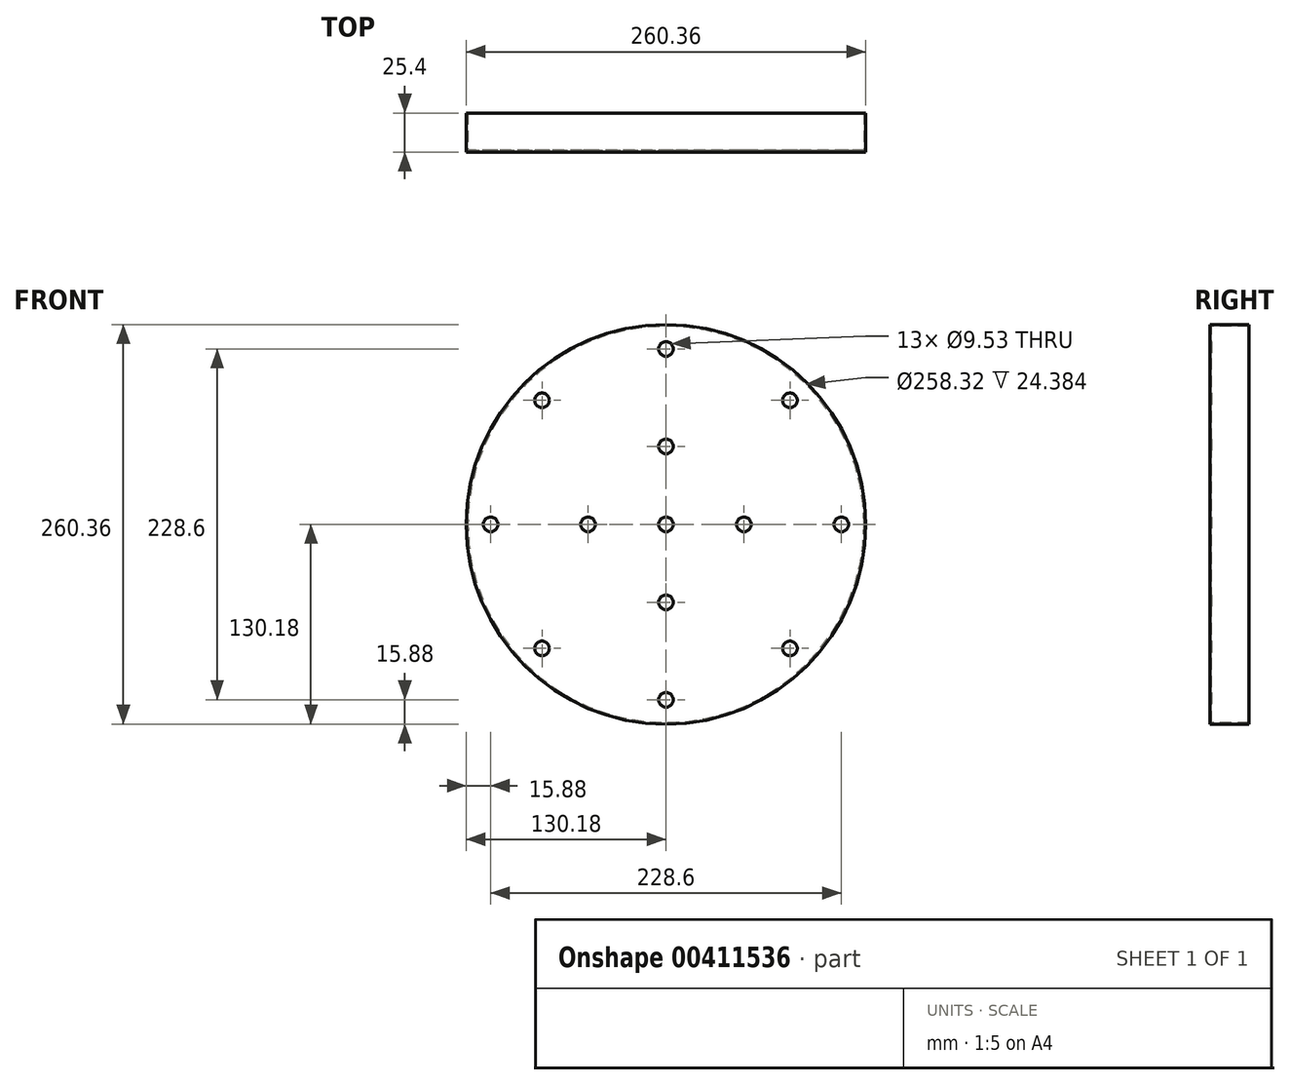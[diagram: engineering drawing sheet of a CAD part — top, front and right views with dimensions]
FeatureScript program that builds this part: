
annotation { "Feature Type Name" : "Feature", "Feature Type Description" : "" }
export const myFeature = defineFeature(function(context is Context, id is Id, definition is map)
    precondition{}
    {
        {
            var Q0;
            Q0=qCreatedBy(makeId("Top.planeOp"),FACE);
            var sketch = newSketch(context, id + "F0", { "sketchPlane" : qUnion([Q0])});
            skLineSegment(sketch, "E0.bottom", {"start": v(0, 0) * mm, "end": v(130.18, 0) * mm});
            skLineSegment(sketch, "E0.top", {"start": v(0, 1.02) * mm, "end": v(129.16, 1.02) * mm});
            skLineSegment(sketch, "E0.left", {"start": v(0, 0) * mm, "end": v(0, 1.02) * mm});
            skLineSegment(sketch, "E1.top", {"start": v(130.18, 25.4) * mm, "end": v(129.16, 25.4) * mm});
            skLineSegment(sketch, "E1.right", {"start": v(129.16, 1.02) * mm, "end": v(129.16, 25.4) * mm});
            skLineSegment(sketch, "E2", {"start": v(130.18, 25.4) * mm, "end": v(130.18, 0) * mm});
            skSolve(sketch);
        }
        {
            var Q0;
            Q0=makeQuery(id+"F0.imprint","IMPRINT",FACE,{"disambiguationData":[TD([[makeQuery(id+"F0.imprint","IMPRINT",EDGE,{"derivedFrom":sQuery(id+"F0.wireOp",EDGE,"E0.bottom")}),1.0]])]});
            var Q1;
            Q1=sQuery(id+"F0.wireOp",EDGE,"E0.left");
            revolve(context, id + "F1", {"entities" : qUnion([Q0]), "axis" : qUnion([Q1]), "revolveType" : RevolveType.FULL});
        }
        {
            var Q0;
            Q0=makeQuery(id+"F1.opRevolve","SWEPT_FACE",FACE,{"disambiguationData":[OSD([sQuery(id+"F0.wireOp",EDGE,"E0.top")])]});
            var sketch = newSketch(context, id + "F2", { "sketchPlane" : qUnion([Q0])});
            skCircle(sketch, "E3", {"center": v(0, 0) * mm, "radius": 4.76 * mm});
            skCircle(sketch, "E4", {"center": v(0, -50.8) * mm, "radius": 4.76 * mm});
            skCircle(sketch, "E5", {"center": v(0, -114.3) * mm, "radius": 4.76 * mm});
            skCircle(sketch, "E6", {"center": v(-50.8, 0) * mm, "radius": 4.76 * mm});
            skCircle(sketch, "E7", {"center": v(0, 50.8) * mm, "radius": 4.76 * mm});
            skCircle(sketch, "E8", {"center": v(-80.82, 80.82) * mm, "radius": 4.76 * mm});
            skCircle(sketch, "E9", {"center": v(80.82, 80.82) * mm, "radius": 4.76 * mm});
            skCircle(sketch, "E10", {"center": v(114.3, 0) * mm, "radius": 4.76 * mm});
            skCircle(sketch, "E11", {"center": v(80.82, -80.82) * mm, "radius": 4.76 * mm});
            skCircle(sketch, "E12", {"center": v(-80.82, -80.82) * mm, "radius": 4.76 * mm});
            skCircle(sketch, "E13", {"center": v(0, 114.3) * mm, "radius": 4.76 * mm});
            skCircle(sketch, "E14", {"center": v(50.8, 0) * mm, "radius": 4.76 * mm});
            skCircle(sketch, "E15", {"center": v(-114.3, 0) * mm, "radius": 4.76 * mm});
            skCircle(sketch, "E16", {"center": v(0, 0) * mm, "radius": 50.8 * mm, "construction": true});
            skCircle(sketch, "E17", {"center": v(0, 0) * mm, "radius": 114.3 * mm, "construction": true});
            skLineSegment(sketch, "E18", {"start": v(-80.82, -80.82) * mm, "end": v(0, 0) * mm, "construction": true});
            skLineSegment(sketch, "E19", {"start": v(0, 0) * mm, "end": v(-114.3, 0) * mm, "construction": true});
            skLineSegment(sketch, "E20", {"start": v(0, 0) * mm, "end": v(-80.82, 80.82) * mm, "construction": true});
            skLineSegment(sketch, "E21", {"start": v(0, 0) * mm, "end": v(80.82, 80.82) * mm, "construction": true});
            skLineSegment(sketch, "E22", {"start": v(0, 0) * mm, "end": v(80.82, -80.82) * mm, "construction": true});
            skSolve(sketch);
        }
        {
            var Q0;
            Q0 = qSketchRegion(id + "F2", true);
            extrude(context, id + "F3", {"entities" : qUnion([Q0]), "operationType" : NewBodyOperationType.REMOVE, "endBound" : BoundingType.THROUGH_ALL, "oppositeDirection" : true, "depth" : 25.4 * mm});
        }
    });
